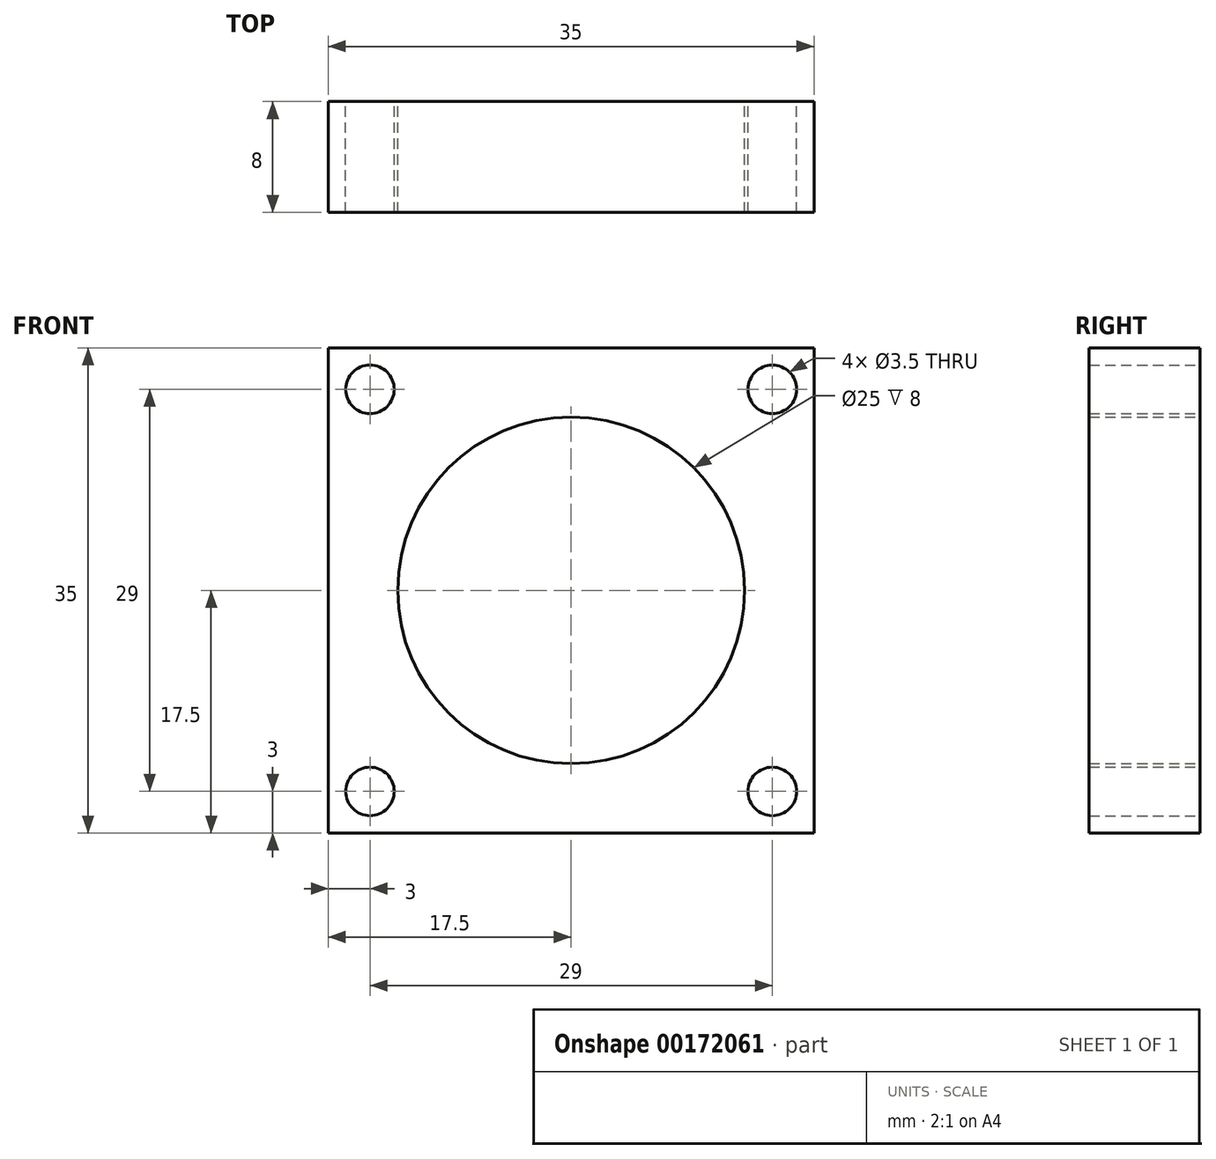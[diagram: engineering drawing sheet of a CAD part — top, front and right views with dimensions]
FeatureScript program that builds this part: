
annotation { "Feature Type Name" : "Feature", "Feature Type Description" : "" }
export const myFeature = defineFeature(function(context is Context, id is Id, definition is map)
    precondition{}
    {
        {
            var Q0;
            Q0=qCreatedBy(makeId("Front.planeOp"),FACE);
            var sketch = newSketch(context, id + "F0", { "sketchPlane" : qUnion([Q0])});
            skCircle(sketch, "E0", {"center": v(0, 0) * mm, "radius": 12.5 * mm});
            skLineSegment(sketch, "E1.bottom", {"start": v(17.5, -17.5) * mm, "end": v(-17.5, -17.5) * mm});
            skLineSegment(sketch, "E1.top", {"start": v(17.5, 17.5) * mm, "end": v(-17.5, 17.5) * mm});
            skLineSegment(sketch, "E1.left", {"start": v(17.5, -17.5) * mm, "end": v(17.5, 17.5) * mm});
            skLineSegment(sketch, "E1.right", {"start": v(-17.5, -17.5) * mm, "end": v(-17.5, 17.5) * mm});
            skLineSegment(sketch, "E2", {"start": v(17.5, 17.5) * mm, "end": v(-17.5, -17.5) * mm, "construction": true});
            skLineSegment(sketch, "E3", {"start": v(-17.5, 17.5) * mm, "end": v(17.5, -17.5) * mm, "construction": true});
            skCircle(sketch, "E4", {"center": v(-14.5, 14.5) * mm, "radius": 1.75 * mm});
            skCircle(sketch, "E5", {"center": v(-14.5, -14.5) * mm, "radius": 1.75 * mm});
            skCircle(sketch, "E6", {"center": v(14.5, -14.5) * mm, "radius": 1.75 * mm});
            skCircle(sketch, "E7", {"center": v(14.5, 14.5) * mm, "radius": 1.75 * mm});
            skSolve(sketch);
        }
        {
            var Q0;
            Q0 = qSketchRegion(id + "F0", true);
            extrude(context, id + "F1", {"entities" : qUnion([Q0]), "depth" : 8 * mm});
        }
    });
